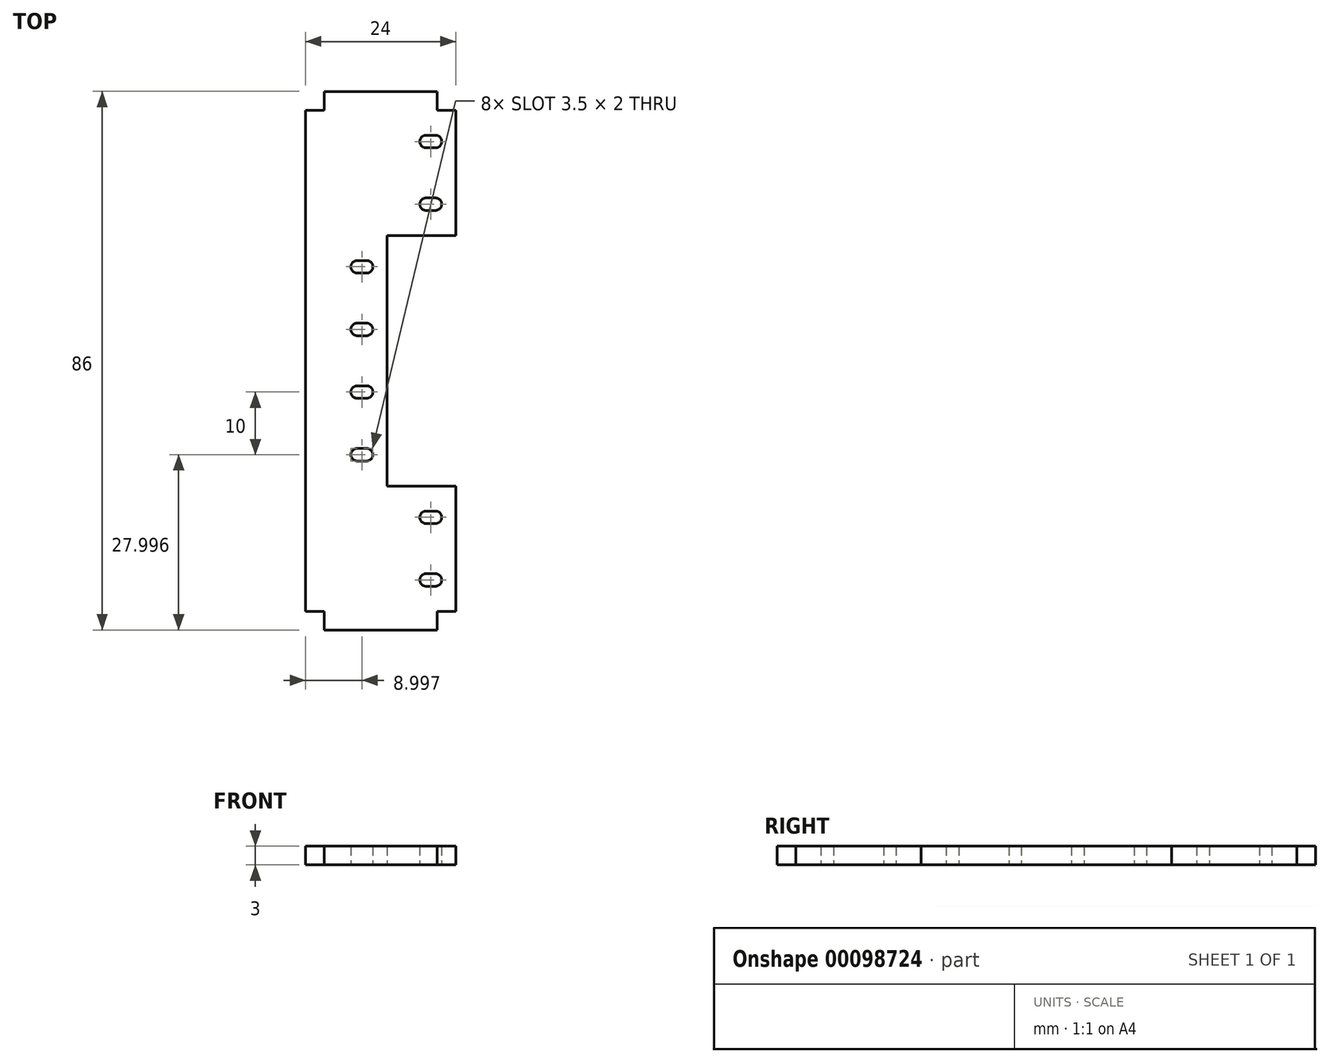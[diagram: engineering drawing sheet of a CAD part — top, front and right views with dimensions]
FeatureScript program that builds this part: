
annotation { "Feature Type Name" : "Feature", "Feature Type Description" : "" }
export const myFeature = defineFeature(function(context is Context, id is Id, definition is map)
    precondition{}
    {
        {
            var Q0;
            Q0=qCreatedBy(makeId("Top.planeOp"),FACE);
            var sketch = newSketch(context, id + "F0", { "sketchPlane" : qUnion([Q0])});
            skLineSegment(sketch, "E0", {"start": v(-52.6, 86.28) * mm, "end": v(-55.6, 86.28) * mm});
            skLineSegment(sketch, "E1", {"start": v(-55.6, 86.28) * mm, "end": v(-55.6, 6.28) * mm});
            skLineSegment(sketch, "E2", {"start": v(-55.6, 6.28) * mm, "end": v(-52.6, 6.28) * mm});
            skLineSegment(sketch, "E3", {"start": v(-52.6, 6.28) * mm, "end": v(-52.6, 3.28) * mm});
            skLineSegment(sketch, "E4", {"start": v(-52.6, 3.28) * mm, "end": v(-34.6, 3.28) * mm});
            skLineSegment(sketch, "E5", {"start": v(-34.6, 3.28) * mm, "end": v(-34.6, 6.28) * mm});
            skLineSegment(sketch, "E6", {"start": v(-34.6, 6.28) * mm, "end": v(-31.6, 6.28) * mm});
            skLineSegment(sketch, "E7", {"start": v(-31.6, 6.28) * mm, "end": v(-31.6, 26.28) * mm});
            skLineSegment(sketch, "E8", {"start": v(-31.6, 26.28) * mm, "end": v(-42.6, 26.28) * mm});
            skLineSegment(sketch, "E9", {"start": v(-42.6, 26.28) * mm, "end": v(-42.6, 66.28) * mm});
            skLineSegment(sketch, "E10", {"start": v(-42.6, 66.28) * mm, "end": v(-31.6, 66.28) * mm});
            skLineSegment(sketch, "E11", {"start": v(-31.6, 66.28) * mm, "end": v(-31.6, 86.28) * mm});
            skLineSegment(sketch, "E12", {"start": v(-31.6, 86.28) * mm, "end": v(-34.6, 86.28) * mm});
            skLineSegment(sketch, "E13", {"start": v(-34.6, 86.28) * mm, "end": v(-34.6, 89.28) * mm});
            skLineSegment(sketch, "E14", {"start": v(-34.6, 89.28) * mm, "end": v(-52.6, 89.28) * mm});
            skLineSegment(sketch, "E15", {"start": v(-52.6, 89.28) * mm, "end": v(-52.6, 86.28) * mm});
            skArc(sketch, "E16", {"start": v(-37.35, 81.28) * mm, "mid": v(-37.06, 80.57) * mm, "end": v(-36.35, 80.28) * mm});
            skLineSegment(sketch, "E17", {"start": v(-36.35, 80.28) * mm, "end": v(-34.85, 80.28) * mm});
            skArc(sketch, "E18", {"start": v(-34.85, 80.28) * mm, "mid": v(-34.15, 80.57) * mm, "end": v(-33.85, 81.28) * mm});
            skArc(sketch, "E19", {"start": v(-33.85, 81.28) * mm, "mid": v(-34.15, 81.98) * mm, "end": v(-34.85, 82.28) * mm});
            skLineSegment(sketch, "E20", {"start": v(-34.85, 82.28) * mm, "end": v(-36.35, 82.28) * mm});
            skArc(sketch, "E21", {"start": v(-36.35, 82.28) * mm, "mid": v(-37.06, 81.98) * mm, "end": v(-37.35, 81.28) * mm});
            skArc(sketch, "E22", {"start": v(-37.35, 71.28) * mm, "mid": v(-37.06, 70.57) * mm, "end": v(-36.35, 70.28) * mm});
            skLineSegment(sketch, "E23", {"start": v(-36.35, 70.28) * mm, "end": v(-34.85, 70.28) * mm});
            skArc(sketch, "E24", {"start": v(-34.85, 70.28) * mm, "mid": v(-34.15, 70.57) * mm, "end": v(-33.85, 71.28) * mm});
            skArc(sketch, "E25", {"start": v(-33.85, 71.28) * mm, "mid": v(-34.15, 71.98) * mm, "end": v(-34.85, 72.28) * mm});
            skLineSegment(sketch, "E26", {"start": v(-34.85, 72.28) * mm, "end": v(-36.35, 72.28) * mm});
            skArc(sketch, "E27", {"start": v(-36.35, 72.28) * mm, "mid": v(-37.06, 71.98) * mm, "end": v(-37.35, 71.28) * mm});
            skArc(sketch, "E28", {"start": v(-48.35, 61.28) * mm, "mid": v(-48.06, 60.57) * mm, "end": v(-47.35, 60.28) * mm});
            skLineSegment(sketch, "E29", {"start": v(-47.35, 60.28) * mm, "end": v(-45.85, 60.28) * mm});
            skArc(sketch, "E30", {"start": v(-45.85, 60.28) * mm, "mid": v(-45.15, 60.57) * mm, "end": v(-44.85, 61.28) * mm});
            skArc(sketch, "E31", {"start": v(-44.85, 61.28) * mm, "mid": v(-45.15, 61.98) * mm, "end": v(-45.85, 62.28) * mm});
            skLineSegment(sketch, "E32", {"start": v(-45.85, 62.28) * mm, "end": v(-47.35, 62.28) * mm});
            skArc(sketch, "E33", {"start": v(-47.35, 62.28) * mm, "mid": v(-48.06, 61.98) * mm, "end": v(-48.35, 61.28) * mm});
            skArc(sketch, "E34", {"start": v(-48.35, 51.28) * mm, "mid": v(-48.06, 50.57) * mm, "end": v(-47.35, 50.28) * mm});
            skLineSegment(sketch, "E35", {"start": v(-47.35, 50.28) * mm, "end": v(-45.85, 50.28) * mm});
            skArc(sketch, "E36", {"start": v(-45.85, 50.28) * mm, "mid": v(-45.15, 50.57) * mm, "end": v(-44.85, 51.28) * mm});
            skArc(sketch, "E37", {"start": v(-44.85, 51.28) * mm, "mid": v(-45.15, 51.98) * mm, "end": v(-45.85, 52.28) * mm});
            skLineSegment(sketch, "E38", {"start": v(-45.85, 52.28) * mm, "end": v(-47.35, 52.28) * mm});
            skArc(sketch, "E39", {"start": v(-47.35, 52.28) * mm, "mid": v(-48.06, 51.98) * mm, "end": v(-48.35, 51.28) * mm});
            skArc(sketch, "E40", {"start": v(-48.35, 41.28) * mm, "mid": v(-48.06, 40.57) * mm, "end": v(-47.35, 40.28) * mm});
            skLineSegment(sketch, "E41", {"start": v(-47.35, 40.28) * mm, "end": v(-45.85, 40.28) * mm});
            skArc(sketch, "E42", {"start": v(-45.85, 40.28) * mm, "mid": v(-45.15, 40.57) * mm, "end": v(-44.85, 41.28) * mm});
            skArc(sketch, "E43", {"start": v(-44.85, 41.28) * mm, "mid": v(-45.15, 41.98) * mm, "end": v(-45.85, 42.28) * mm});
            skLineSegment(sketch, "E44", {"start": v(-45.85, 42.28) * mm, "end": v(-47.35, 42.28) * mm});
            skArc(sketch, "E45", {"start": v(-47.35, 42.28) * mm, "mid": v(-48.06, 41.98) * mm, "end": v(-48.35, 41.28) * mm});
            skArc(sketch, "E46", {"start": v(-48.35, 31.28) * mm, "mid": v(-48.06, 30.57) * mm, "end": v(-47.35, 30.28) * mm});
            skLineSegment(sketch, "E47", {"start": v(-47.35, 30.28) * mm, "end": v(-45.85, 30.28) * mm});
            skArc(sketch, "E48", {"start": v(-45.85, 30.28) * mm, "mid": v(-45.15, 30.57) * mm, "end": v(-44.85, 31.28) * mm});
            skArc(sketch, "E49", {"start": v(-44.85, 31.28) * mm, "mid": v(-45.15, 31.98) * mm, "end": v(-45.85, 32.28) * mm});
            skLineSegment(sketch, "E50", {"start": v(-45.85, 32.28) * mm, "end": v(-47.35, 32.28) * mm});
            skArc(sketch, "E51", {"start": v(-47.35, 32.28) * mm, "mid": v(-48.06, 31.98) * mm, "end": v(-48.35, 31.28) * mm});
            skArc(sketch, "E52", {"start": v(-37.35, 21.28) * mm, "mid": v(-37.06, 20.57) * mm, "end": v(-36.35, 20.28) * mm});
            skLineSegment(sketch, "E53", {"start": v(-36.35, 20.28) * mm, "end": v(-34.85, 20.28) * mm});
            skArc(sketch, "E54", {"start": v(-34.85, 20.28) * mm, "mid": v(-34.15, 20.57) * mm, "end": v(-33.85, 21.28) * mm});
            skArc(sketch, "E55", {"start": v(-33.85, 21.28) * mm, "mid": v(-34.15, 21.98) * mm, "end": v(-34.85, 22.28) * mm});
            skLineSegment(sketch, "E56", {"start": v(-34.85, 22.28) * mm, "end": v(-36.35, 22.28) * mm});
            skArc(sketch, "E57", {"start": v(-36.35, 22.28) * mm, "mid": v(-37.06, 21.98) * mm, "end": v(-37.35, 21.28) * mm});
            skArc(sketch, "E58", {"start": v(-37.35, 11.28) * mm, "mid": v(-37.06, 10.57) * mm, "end": v(-36.35, 10.28) * mm});
            skLineSegment(sketch, "E59", {"start": v(-36.35, 10.28) * mm, "end": v(-34.85, 10.28) * mm});
            skArc(sketch, "E60", {"start": v(-34.85, 10.28) * mm, "mid": v(-34.15, 10.57) * mm, "end": v(-33.85, 11.28) * mm});
            skArc(sketch, "E61", {"start": v(-33.85, 11.28) * mm, "mid": v(-34.15, 11.98) * mm, "end": v(-34.85, 12.28) * mm});
            skLineSegment(sketch, "E62", {"start": v(-34.85, 12.28) * mm, "end": v(-36.35, 12.28) * mm});
            skArc(sketch, "E63", {"start": v(-36.35, 12.28) * mm, "mid": v(-37.06, 11.98) * mm, "end": v(-37.35, 11.28) * mm});
            skSolve(sketch);
        }
        {
            var Q0;
            Q0=makeQuery(id+"F0.imprint","IMPRINT",FACE,{"disambiguationData":[TD([[makeQuery(id+"F0.imprint","IMPRINT",EDGE,{"derivedFrom":sQuery(id+"F0.wireOp",EDGE,"E0")}),1.0]])]});
            extrude(context, id + "F1", {"entities" : qUnion([Q0]), "depth" : 3 * mm, "symmetric" : true});
        }
    });
